# Revit family: Grinder_Pump-High_Flow-Commercial-Hazardous_Environment-Zoeller-X71_Vertical_Series
name_source: partatom
category: Mechanical Equipment
units: mm (PartAtom-declared; Revit-internal decimal feet)

## family parameters
Always vertical = No
Cut with Voids When Loaded = No
OmniClass Number = 23.60.30.21
OmniClass Title = Pumps
Part Type = Normal
Room Calculation Point = No
Round Connector Dimension = Use Radius
Shared = Yes
Work Plane-Based = Yes

## types (14) — shared parameters
Assembly Code = D2090
Default Elevation = 0"
Description = Commercial Grinder Pump for Hazardous location for Class I, Division 1, Groups C and D
Discharge Diameter = 2"
Discharge Radius = 1"
Flange = ANSI B16.1
Height = 33 1/2"
Hertz = 60
Impeller Type = Ductile Iron Vortex, Bronze Optional
Installation Type = Floor Mounted
Insulation = Class F
Length = 13 13/16"
Manufacturer = Zoeller
Material = Cast Iron-Zoeller-Powder Coated Epoxy
Max. Stator Temp. = 311 °F
Max. Water Temp. = 104 °F
Mechanical Seals = Tandem carbon/ceramic upper and silicon carbide/silicon carbide lower
Moisture Detection = Thermal Sensors with Automatic Reset Moisture Sensing Probes
Motor Design Letter = NEMA B (3 Ph), NEMA L (1 Ph)
Motor Shaft = 416 S.S.
Motor Thermal Shutoff = Thermal Sensors with Automatic Reset Moisture Sensing Probes
Motor Type = Submersible Explosion Proof
O-Rings = Buna-N
O-Rings (Optional) Viton = No
Operation = Non-Automatic
Power Cord = #12-4 SO (Models with a FLA greater than 20 amps use #8-4 gauge power cord)
Price = Prices may vary. Please consult Manufacturer Representative for most up-to-date price list.
Product Documentation Link = http://cdn.qleapahead.com
Product Page URL = http://www.zoellerengprod.com
RPM = 3450
Service Factor = 1.2
Shaft Seal (Standard) = Carbon/Ceramic
Shaft Seal Lower (Options) = Carbon/Silicon Carbide, Silicon Carbide/Silicon Carbide
Shaft Seal Upper (Options) = Carbon/Silicon Carbide, Silicon Carbide/Silicon Carbide
Shipping Weight = 245 lbs (111 kg)
Tandem Seals = Standard
Trimmed Impeller = No
Type SOW Power Cord Length = 300"
URL = http://www.zoellerengprod.com
Warranty Information = 36 Months (Limited)
Waste Connection = Yes
Width = 11 3/4"

## per-type parameters (varying)
| type | Amps | Apparent Load | Flow @ 5' | Locked Rotor Amps (Voltage Dependant) | Max. Head | Maximum KW Input | Model | Motor | NEC Locked Rotor Code | Phase | Voltage |
| X7110-2" 230V/1Ph/23.6A/3HP | 24 A | 5428 VA | 140 GPM | 132 | 59' | 5.3 | X7110-2" | 3.0 HP | M (1 Ph), G (3 Ph) | 1 | 230 V |
| X7110-2" 200V/3Ph/17.3A/3HP | 17 A | 3460 VA | 140 GPM | 66 | 59' | 5.3 | X7110-2" | 3.0 HP | M (1 Ph), G (3 Ph) | 3 | 200 V |
| X7110-2" 230V/3Ph/15.1A/3HP | 15 A | 3473 VA | 140 GPM | 57 | 59' | 5.3 | X7110-2" | 3.0 HP | M (1 Ph), G (3 Ph) | 3 | 230 V |
| X7110-2" 460V/3Ph/7.5A/3HP | 8 A | 3450 VA | 140 GPM | 28.5 | 59' | 5.3 | X7110-2" | 3.0 HP | M (1 Ph), G (3 Ph) | 3 | 460 V |
| X7110-2" 575V/3Ph/6.0A/3HP | 6 A | 3450 VA | 140 GPM | 25.2 | 59' | 5.3 | X7110-2" | 3.0 HP | M (1 Ph), G (3 Ph) | 3 | 575 V |
| X7111-2" 230V/1Ph/28.0A/5HP | 28 A | 6440 VA | 167 GPM | 132 | 92' | 6.4 | X7111-2" | 5.0 HP | M (1 Ph), G (3 Ph) | 1 | 230 V |
| X7111-2" 200V/3Ph/20.7A/5HP | 21 A | 4140 VA | 167 GPM | 94 | 92' | 6.4 | X7111-2" | 5.0 HP | M (1 Ph), G (3 Ph) | 3 | 200 V |
| X7111-2" 230V/3Ph/18.0A/5HP | 18 A | 4140 VA | 167 GPM | 82 | 92' | 6.4 | X7111-2" | 5.0 HP | M (1 Ph), G (3 Ph) | 3 | 230 V |
| X7111-2" 460V/3Ph/9.0A/5HP | 9 A | 4140 VA | 167 GPM | 41 | 92' | 6.4 | X7111-2" | 5.0 HP | M (1 Ph), G (3 Ph) | 3 | 460 V |
| X7111-2" 575V/3Ph/7.2A/5HP | 7 A | 4140 VA | 167 GPM | 36 | 92' | 6.4 | X7111-2" | 5.0 HP | M (1 Ph), G (3 Ph) | 3 | 575 V |
| X7112-2" 200V/3Ph/25.3A/7.5HP | 25 A | 5060 VA | 175 GPM | 94 | 122' | 8 | X7112-2" | 7.5 HP | D | 3 | 200 V |
| X7112-2" 230V/3Ph/22.0A/7.5HP | 22 A | 5060 VA | 175 GPM | 82 | 122' | 8 | X7112-2" | 7.5 HP | D | 3 | 230 V |
| X7112-2" 460V/3Ph/11.0A/7.5HP | 11 A | 5060 VA | 175 GPM | 41 | 122' | 8 | X7112-2" | 7.5 HP | D | 3 | 460 V |
| X7112-2" 575V/3Ph/9.0A/7.5HP | 9 A | 5175 VA | 175 GPM | 36 | 122' | 8 | X7112-2" | 7.5 HP | D | 3 | 575 V |

## geometry (parser evidence)
native form markers: Sweep x3
no freeform markers — native parametric forms only
